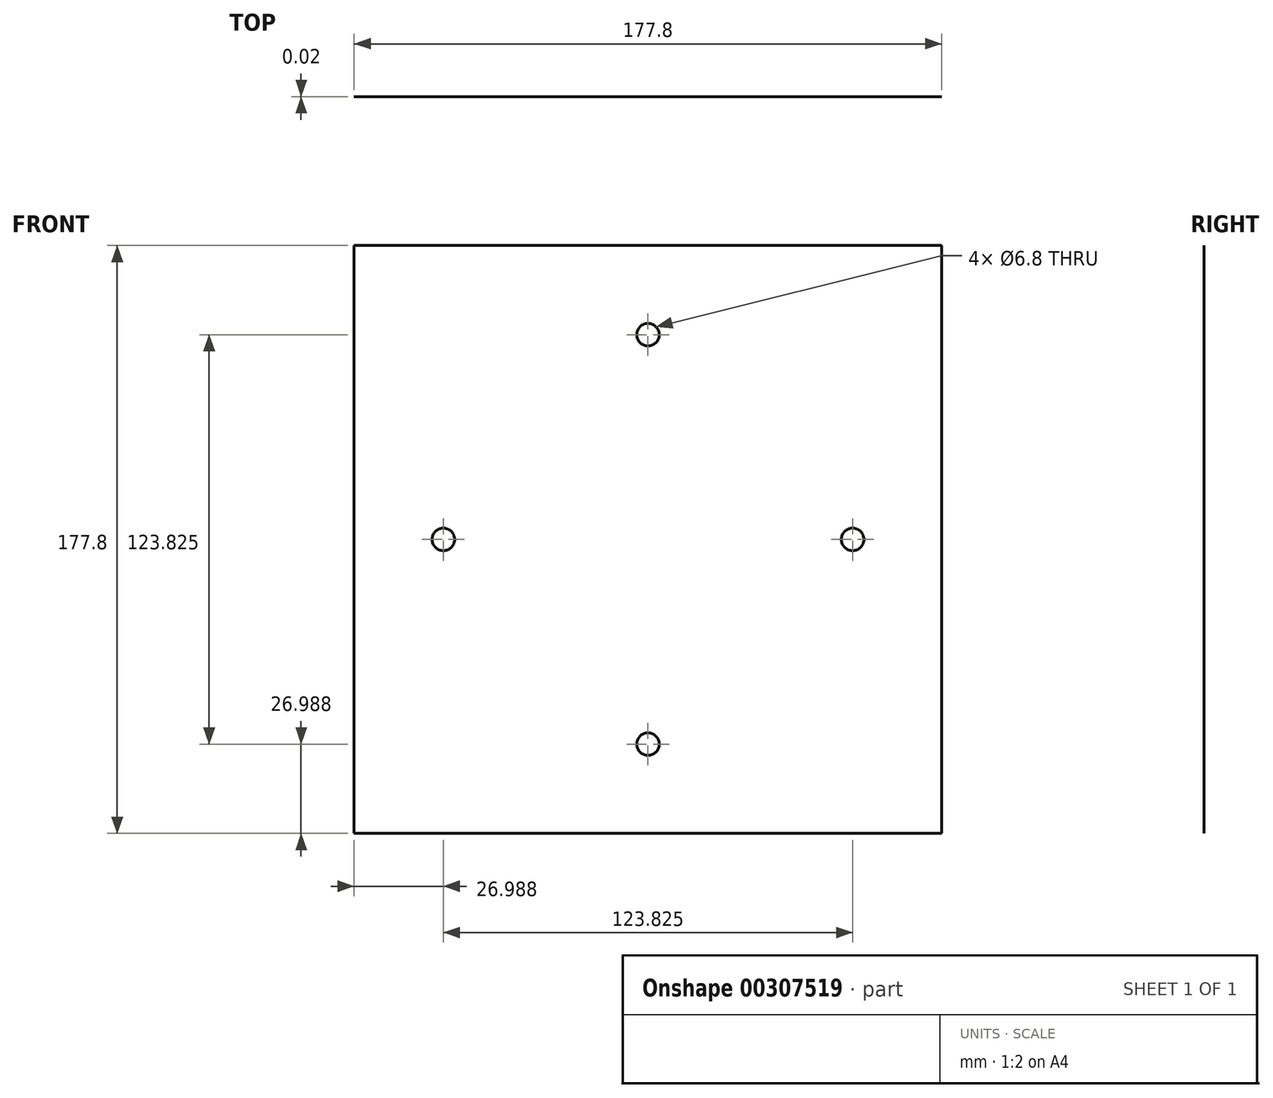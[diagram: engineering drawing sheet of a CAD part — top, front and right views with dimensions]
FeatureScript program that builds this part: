
annotation { "Feature Type Name" : "Feature", "Feature Type Description" : "" }
export const myFeature = defineFeature(function(context is Context, id is Id, definition is map)
    precondition{}
    {
        {
            var Q0;
            Q0=qCreatedBy(makeId("Front.planeOp"),FACE);
            var sketch = newSketch(context, id + "F0", { "sketchPlane" : qUnion([Q0])});
            skLineSegment(sketch, "E0.bottom", {"start": v(88.9, -88.9) * mm, "end": v(-88.9, -88.9) * mm});
            skLineSegment(sketch, "E0.top", {"start": v(88.9, 88.9) * mm, "end": v(-88.9, 88.9) * mm});
            skLineSegment(sketch, "E0.left", {"start": v(88.9, -88.9) * mm, "end": v(88.9, 88.9) * mm});
            skLineSegment(sketch, "E0.right", {"start": v(-88.9, -88.9) * mm, "end": v(-88.9, 88.9) * mm});
            skPoint(sketch, "E1", {"position": v(0, 0) * mm});
            skPoint(sketch, "E2", {"position": v(-61.91, 0) * mm});
            skPoint(sketch, "E3", {"position": v(61.91, 0) * mm});
            skPoint(sketch, "E4", {"position": v(0, -61.91) * mm});
            skPoint(sketch, "E5", {"position": v(0, 61.91) * mm});
            skSolve(sketch);
        }
        {
            var Q0;
            Q0=qSketchRegion(id+"F0",true);
            extrude(context, id + "F1", {"entities" : qUnion([Q0]), "depth" : 1 / 50.8 * mm});
        }
        {
            var Q0;
            Q0=sQuery(id+"F0.wireOp",VERTEX,"E2");
            var Q1;
            Q1=sQuery(id+"F0.wireOp",VERTEX,"E5");
            var Q2;
            Q2=sQuery(id+"F0.wireOp",VERTEX,"E3");
            var Q3;
            Q3=sQuery(id+"F0.wireOp",VERTEX,"E4");
            var Q4;
            Q4=makeQuery(id+"F1.opExtrude","SWEPT_BODY",BODY,{"disambiguationData":[OSD([sQuery(id+"F0.wireOp",EDGE,"E0.bottom"),sQuery(id+"F0.wireOp",EDGE,"E0.top"),sQuery(id+"F0.wireOp",EDGE,"E0.left"),sQuery(id+"F0.wireOp",EDGE,"E0.right")])]});
            hole(context, id + "F2", {"style" : HoleStyle.SIMPLE, "endStyle" : HoleEndStyle.THROUGH, "oppositeDirection" : true, "standardTappedOrClearance" : lookupTablePath({ "standard" : "ISO", "engagement" : "75%", "pitch" : "1.25 mm", "size" : "M8", "type" : "Tapped" }), "standardBlindInLast" : lookupTablePath({ "standard" : "ISO", "engagement" : "75%", "pitch" : "1.25 mm", "size" : "M8", "type" : "Tapped" }), "holeDiameter" : 6.8 * mm, "showTappedDepth" : true, "tappedDepth" : 12.7 * mm, "tapClearance" : 3, "locations" : qUnion([Q0, Q1, Q2, Q3]), "scope" : qUnion([Q4]), "majorDiameter" : 8 * mm});
        }
    });
